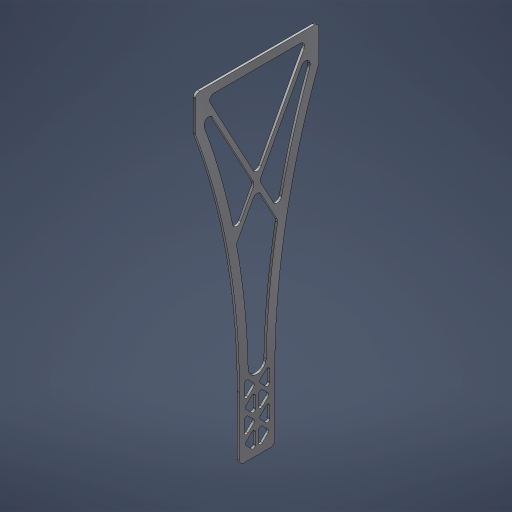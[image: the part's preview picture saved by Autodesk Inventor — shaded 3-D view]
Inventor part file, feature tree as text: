
AUTODESK INVENTOR PART (.ipt)
format: ipt  version: 2024.3 (Build 283343000, 343)  size: 467,456 bytes
history: native  units: mm (DEFAULTED — no unit token found)
features: sheet_metal_op x3, sketch x3, other x3, mirror x2, chamfer x2, projected_geometry x1
ambient origin geometry x8: Origin, YZ Plane, XZ Plane, XY Plane, X Axis, Y Axis, Z Axis, Center Point
bodies: Body1 (feature_tree)
feature tree (14):
  sheet_metal_op  "Face1"
  sheet_metal_op  "Face2"
  mirror  "Mirror2"
  mirror  "Mirror3"
  chamfer  "Corner Round3"
  chamfer  "Corner Round2"
  sketch  "Sketch2"  dims[d6=177.8mm]
  other  "Plate1"
  sketch  "Sketch5"  dims[d7=596.9mm]
  projected_geometry  "Projected Loop2"
  other  "Plate3"
  sheet_metal_op  "Bend2"
  sketch  "Sketch6"  dims[d10=50.8mm d11=25.4mm d12=127.0mm d13=3.175mm d53=1016.0mm d54=12.7mm d59=6.35mm d60=4.7625mm d61=3.175mm d62=1.5875mm d63=6.35mm d64=4.7625mm d65=355.6mm d66=6.35mm d67=15.875mm d68=2.38125mm d69=7.14375mm d70=4.7625mm d71=38.485192mm d72=6.735192mm d73=20.0mm d75=45.220384mm d76=10.0mm d78=25.4mm d80=6.35mm d81=3.175mm d82=0.0mm d83=3.175mm]
  other  "Cut3"
